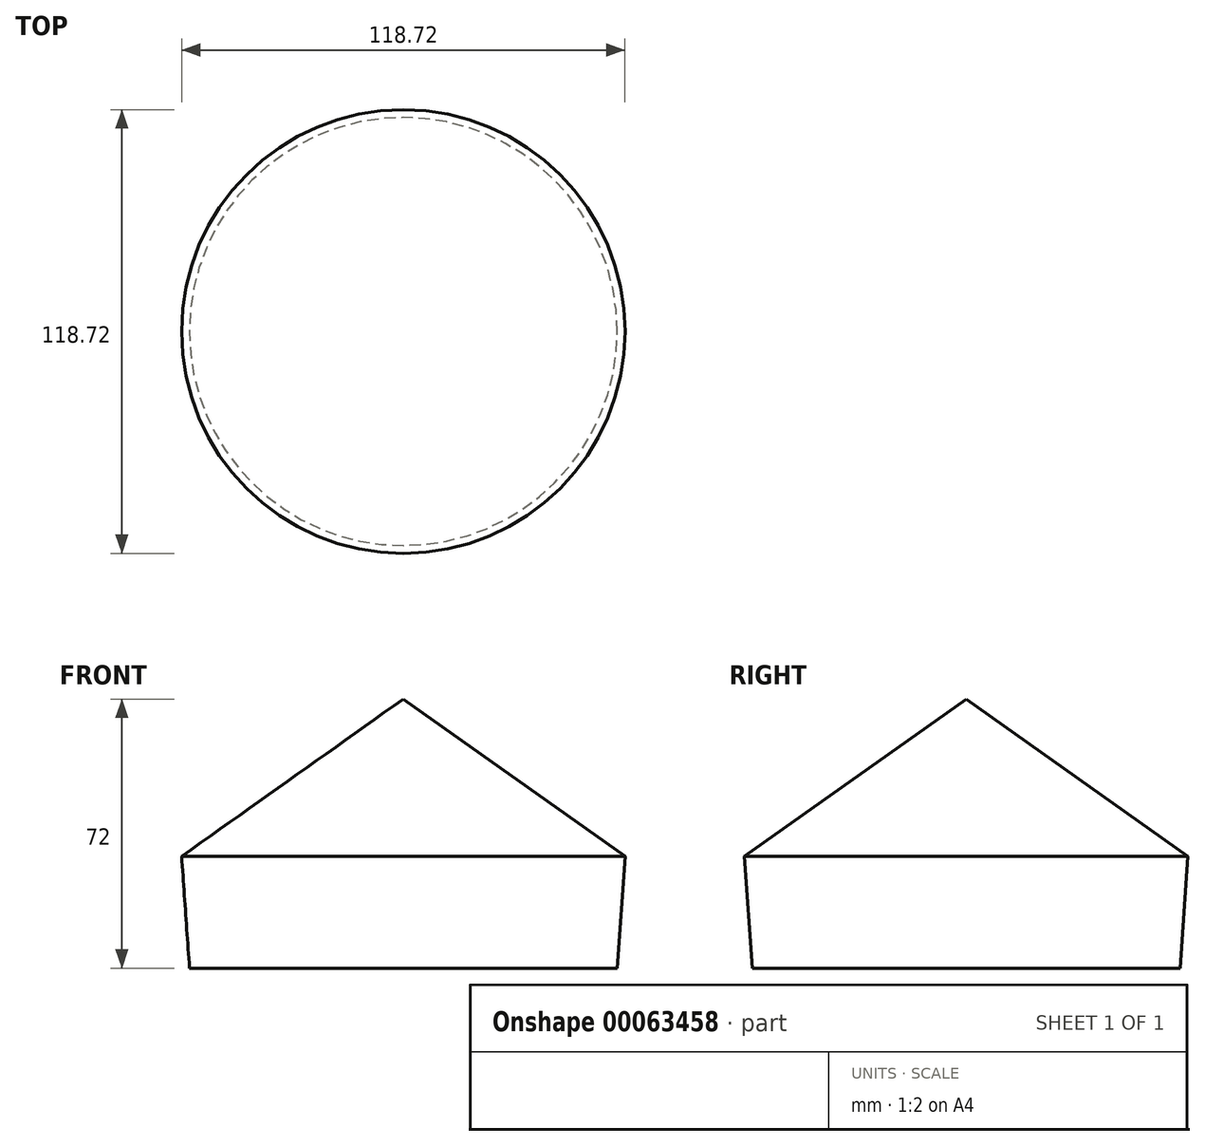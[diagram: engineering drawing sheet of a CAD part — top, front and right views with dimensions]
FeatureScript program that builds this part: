
annotation { "Feature Type Name" : "Feature", "Feature Type Description" : "" }
export const myFeature = defineFeature(function(context is Context, id is Id, definition is map)
    precondition{}
    {
        {
            var Q0;
            Q0=qCreatedBy(makeId("Right.planeOp"),FACE);
            var sketch = newSketch(context, id + "F0", { "sketchPlane" : qUnion([Q0])});
            skLineSegment(sketch, "E0", {"start": v(-57.25, 0) * mm, "end": v(0, 0) * mm});
            skLineSegment(sketch, "E1", {"start": v(0, 0) * mm, "end": v(0, 72) * mm});
            skLineSegment(sketch, "E2", {"start": v(0, 72) * mm, "end": v(-59.36, 29.93) * mm});
            skLineSegment(sketch, "E3", {"start": v(-59.36, 29.93) * mm, "end": v(-57.25, 0) * mm});
            skSolve(sketch);
        }
        {
            var Q0;
            Q0=makeQuery(id+"F0.imprint","IMPRINT",FACE,{"disambiguationData":[TD([[makeQuery(id+"F0.imprint","IMPRINT",EDGE,{"derivedFrom":sQuery(id+"F0.wireOp",EDGE,"E0")}),1.0]])]});
            var Q1;
            Q1=sQuery(id+"F0.wireOp",EDGE,"E1");
            revolve(context, id + "F1", {"entities" : qUnion([Q0]), "axis" : qUnion([Q1]), "revolveType" : RevolveType.FULL});
        }
    });
